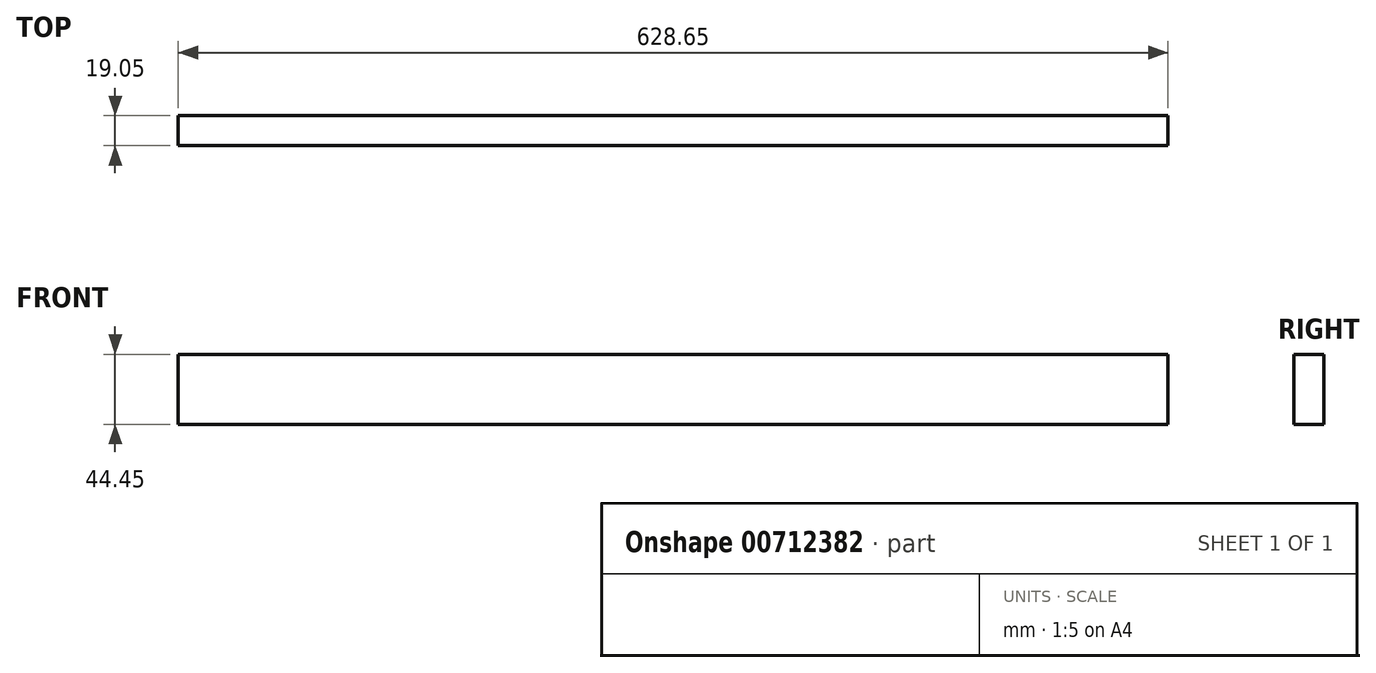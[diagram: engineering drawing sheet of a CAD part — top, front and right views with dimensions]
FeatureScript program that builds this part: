
annotation { "Feature Type Name" : "Feature", "Feature Type Description" : "" }
export const myFeature = defineFeature(function(context is Context, id is Id, definition is map)
    precondition{}
    {
        {
            var Q0;
            Q0=qCreatedBy(makeId("Front.planeOp"),FACE);
            var sketch = newSketch(context, id + "F0", { "sketchPlane" : qUnion([Q0])});
            skLineSegment(sketch, "E0.bottom", {"start": v(0, 0) * mm, "end": v(628.65, 0) * mm});
            skLineSegment(sketch, "E0.top", {"start": v(0, 44.45) * mm, "end": v(628.65, 44.45) * mm});
            skLineSegment(sketch, "E0.left", {"start": v(0, 0) * mm, "end": v(0, 44.45) * mm});
            skLineSegment(sketch, "E0.right", {"start": v(628.65, 0) * mm, "end": v(628.65, 44.45) * mm});
            skSolve(sketch);
        }
        {
            var Q0;
            Q0=makeQuery(id+"F0.imprint","IMPRINT",FACE,{"disambiguationData":[TD([[makeQuery(id+"F0.imprint","IMPRINT",EDGE,{"derivedFrom":sQuery(id+"F0.wireOp",EDGE,"E0.bottom")}),1.0]])]});
            extrude(context, id + "F1", {"entities" : qUnion([Q0]), "depth" : 19.05 * mm, "offsetDistance" : 25.4 * mm});
        }
    });
